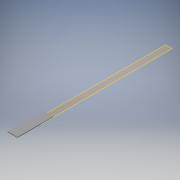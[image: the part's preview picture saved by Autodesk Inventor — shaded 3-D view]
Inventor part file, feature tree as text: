
AUTODESK INVENTOR PART (.ipt)
format: ipt  version: 2016 (Build 200138000, 138)  size: 104,448 bytes
history: native  units: mm
features: plane x1, extrude x1, sketch x1
ambient origin geometry x8: Origin, YZ Plane, XZ Plane, XY Plane, X Axis, Y Axis, Z Axis, Center Point
bodies: Solid1 (feature_tree)
feature tree (3):
  plane  "Work Plane1"
  extrude  "Extrusion1"  Depth=330.0mm
  sketch  "Sketch1"  dims[d0=90.0mm d1=330.0mm d2=6.0mm d3=0.0mm d4=100.0mm d5=70.0mm d6=42.0mm d7=180.0mm d8=52.0mm d9=44.0mm]
